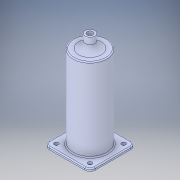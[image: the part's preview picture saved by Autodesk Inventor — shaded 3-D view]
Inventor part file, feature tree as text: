
AUTODESK INVENTOR PART (.ipt)
format: ipt  version: 2018 (Build 220112000, 112)  size: 210,944 bytes
history: native  units: in
note: dims shown in document units (in); Inventor stores cm internally (conversion verified against a paired STEP export)
features: extrude x6, sketch x4, fillet x3, projected_geometry x3, other x1
ambient origin geometry x8: Origin, YZ Plane, XZ Plane, XY Plane, X Axis, Y Axis, Z Axis, Center Point
bodies: Solid1 (feature_tree)
feature tree (17):
  extrude  "Extrusion1"  TaperAngle=0.0deg  [1 undecoded]
  sketch  "Sketch2"  dims[d4=0.3937in d5=0.0in d6=1.0in d7=0.0in]
  extrude  "Extrusion2"  Depth=1.0in TaperAngle=0.0deg
  extrude  "Extrusion3"  Depth=0.9252in
  sketch  "Sketch3"  dims[d8=2.0in d9=0.0in d10=0.9252in]
  extrude  "Extrusion4"  Depth=2.0in TaperAngle=0.0deg
  extrude  "Extrusion5"  Depth=0.5in
  extrude  "Extrusion6"  Depth=1.0in
  fillet  "Fillet2"  [1 undecoded]
  fillet  "Fillet3"  [1 undecoded]
  fillet  "Fillet1"  [1 undecoded]
  sketch  "Sketch1"  dims[d0=0.0in d1=0.0in d2=0.0in d3=0.0in]
  projected_geometry  "Projected Loop1"
  projected_geometry  "Projected Loop2"
  projected_geometry  "Projected Loop3"
  sketch  "Sketch4"  dims[d11=0.45in d12=2.0in d13=0.0in d14=0.5in d15=1.0in]
  other  "Ø8.0mm Dowel Hole1"
note: 4 required parameter values undecoded (feature->parameter linkage not recoverable at this tier; creation-order binding heuristic only, values carry confidence <= 0.55)
